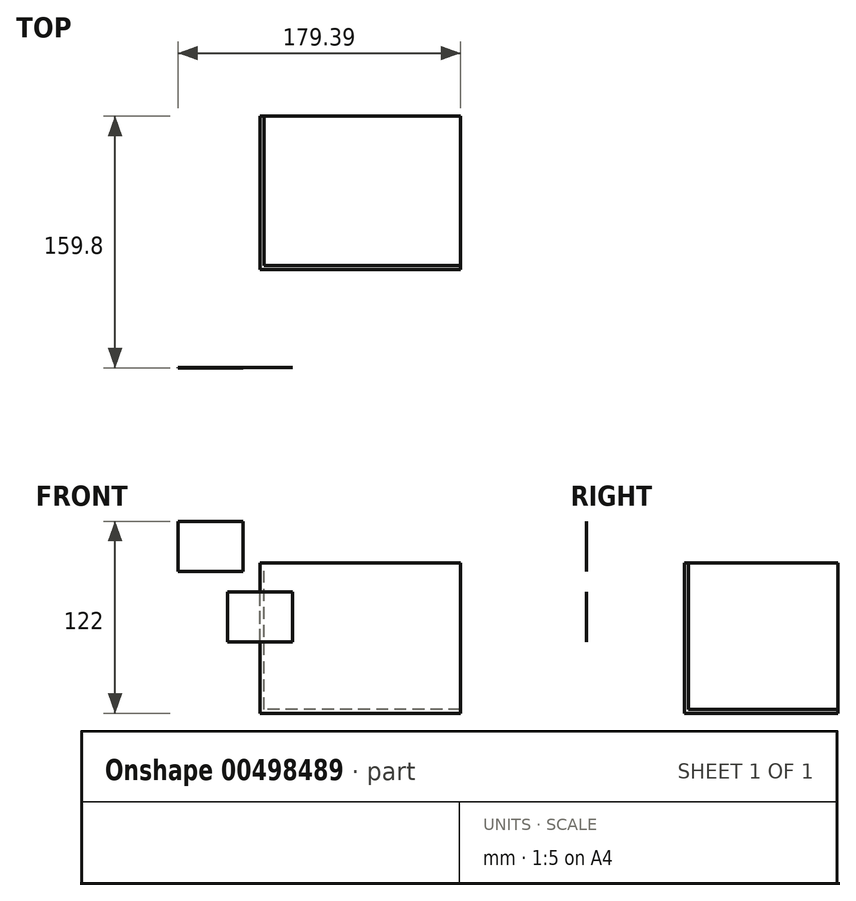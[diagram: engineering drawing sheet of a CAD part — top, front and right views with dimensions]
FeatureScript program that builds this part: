
annotation { "Feature Type Name" : "Feature", "Feature Type Description" : "" }
export const myFeature = defineFeature(function(context is Context, id is Id, definition is map)
    precondition{}
    {
        {
            var Q0;
            Q0=qCreatedBy(makeId("Front.planeOp"),FACE);
            var sketch = newSketch(context, id + "F0", { "sketchPlane" : qUnion([Q0])});
            skLineSegment(sketch, "E0.bottom", {"start": v(-52.02, 29.05) * mm, "end": v(-10.72, 29.05) * mm});
            skLineSegment(sketch, "E0.top", {"start": v(-52.02, 60.82) * mm, "end": v(-10.72, 60.82) * mm});
            skLineSegment(sketch, "E0.left", {"start": v(-52.02, 29.05) * mm, "end": v(-52.02, 60.82) * mm});
            skLineSegment(sketch, "E0.right", {"start": v(-10.72, 29.05) * mm, "end": v(-10.72, 60.82) * mm});
            skSolve(sketch);
        }
        {
            var Q0;
            Q0=makeQuery(id+"F0.imprint","IMPRINT",FACE,{"disambiguationData":[TD([[makeQuery(id+"F0.imprint","IMPRINT",EDGE,{"derivedFrom":sQuery(id+"F0.wireOp",EDGE,"E0.bottom")}),1.0]])]});
            extrude(context, id + "F1", {"entities" : qUnion([Q0]), "depth" : 0.01 * mm});
        }
        {
            var Q0;
            Q0=qCreatedBy(makeId("Right.planeOp"),FACE);
            var sketch = newSketch(context, id + "F2", { "sketchPlane" : qUnion([Q0])});
            skLineSegment(sketch, "E1.bottom", {"start": v(62.37, -61.18) * mm, "end": v(159.8, -61.18) * mm});
            skLineSegment(sketch, "E1.top", {"start": v(62.37, 34.23) * mm, "end": v(159.8, 34.23) * mm});
            skLineSegment(sketch, "E1.left", {"start": v(62.37, -61.18) * mm, "end": v(62.37, 34.23) * mm});
            skLineSegment(sketch, "E1.right", {"start": v(159.8, -61.18) * mm, "end": v(159.8, 34.23) * mm});
            skSolve(sketch);
        }
        {
            var Q0;
            Q0 = qSketchRegion(id + "F2", true);
            extrude(context, id + "F3", {"bodyType" : ToolBodyType.SURFACE, "surfaceEntities" : qUnion([Q0]), "depth" : 127.37 * mm});
        }
        {
            var Q0;
            Q0=makeQuery(id+"F3.opExtrude","SWEPT_FACE",FACE,{"disambiguationData":[OSD([sQuery(id+"F2.wireOp",EDGE,"E1.top")])]});
            var Q1;
            Q1=makeQuery(id+"F3.opExtrude","CAP_FACE",FACE,{"disambiguationData":[OSD([sQuery(id+"F2.wireOp",EDGE,"E1.bottom"),sQuery(id+"F2.wireOp",EDGE,"E1.top"),sQuery(id+"F2.wireOp",EDGE,"E1.left"),sQuery(id+"F2.wireOp",EDGE,"E1.right")])],"isStart":false});
            var Q2;
            Q2=makeQuery(id+"F3.opExtrude","SWEPT_FACE",FACE,{"disambiguationData":[OSD([sQuery(id+"F2.wireOp",EDGE,"E1.right")])]});
            shell(context, id + "F4", {"entities" : qUnion([Q0, Q1, Q2]), "thickness" : 2.5 * mm});
        }
        {
            var Q0;
            Q0=qCreatedBy(makeId("Front.planeOp"),FACE);
            var sketch = newSketch(context, id + "F5", { "sketchPlane" : qUnion([Q0])});
            skLineSegment(sketch, "E2.bottom", {"start": v(-20.65, -15.88) * mm, "end": v(20.65, -15.88) * mm});
            skLineSegment(sketch, "E2.top", {"start": v(-20.65, 15.88) * mm, "end": v(20.65, 15.88) * mm});
            skLineSegment(sketch, "E2.left", {"start": v(-20.65, -15.88) * mm, "end": v(-20.65, 15.88) * mm});
            skLineSegment(sketch, "E2.right", {"start": v(20.65, -15.88) * mm, "end": v(20.65, 15.88) * mm});
            skSolve(sketch);
        }
        {
            var Q0;
            Q0 = qSketchRegion(id + "F5", true);
            var Q1;
            Q1=makeQuery(id+"F5.imprint","IMPRINT",FACE,{"disambiguationData":[TD([[makeQuery(id+"F5.imprint","IMPRINT",EDGE,{"derivedFrom":sQuery(id+"F5.wireOp",EDGE,"E2.bottom")}),1.0]])]});
            extrude(context, id + "F6", {"entities" : qUnion([Q0, Q1]), "depth" : 0 * mm});
        }
    });
